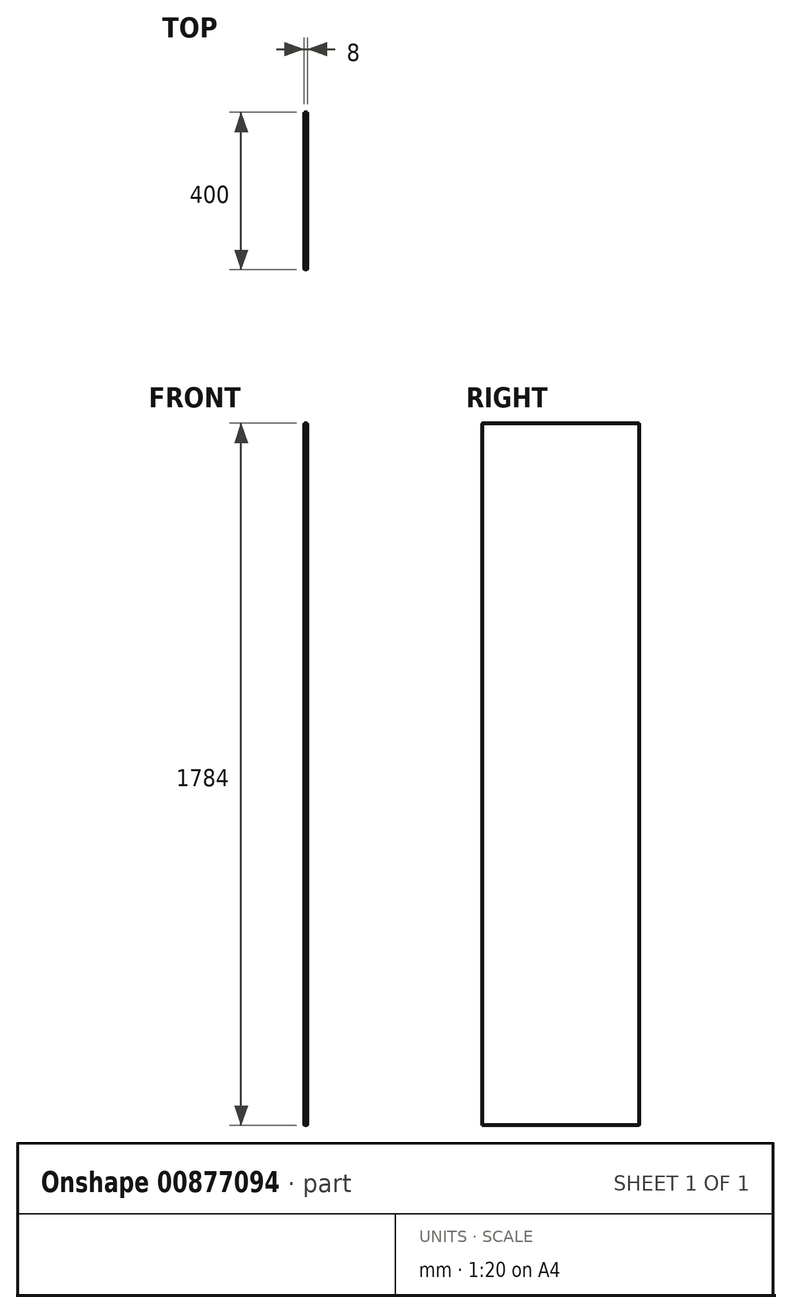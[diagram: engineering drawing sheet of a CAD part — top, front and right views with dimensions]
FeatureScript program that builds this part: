
annotation { "Feature Type Name" : "Feature", "Feature Type Description" : "" }
export const myFeature = defineFeature(function(context is Context, id is Id, definition is map)
    precondition{}
    {
        {
            var Q0;
            Q0=qCreatedBy(makeId("Right.planeOp"),FACE);
            var sketch = newSketch(context, id + "F0", { "sketchPlane" : qUnion([Q0])});
            skLineSegment(sketch, "E0.bottom", {"start": v(200, 892) * mm, "end": v(-200, 892) * mm});
            skLineSegment(sketch, "E0.top", {"start": v(200, -892) * mm, "end": v(-200, -892) * mm});
            skLineSegment(sketch, "E0.left", {"start": v(200, 892) * mm, "end": v(200, -892) * mm});
            skLineSegment(sketch, "E0.right", {"start": v(-200, 892) * mm, "end": v(-200, -892) * mm});
            skPoint(sketch, "E0.middle", {"position": v(0, 0) * mm});
            skSolve(sketch);
        }
        {
            var Q0;
            Q0=makeQuery(id+"F0.imprint","IMPRINT",FACE,{"disambiguationData":[TD([[makeQuery(id+"F0.imprint","IMPRINT",EDGE,{"derivedFrom":sQuery(id+"F0.wireOp",EDGE,"E0.bottom")}),1.0]])]});
            extrude(context, id + "F1", {"entities" : qUnion([Q0]), "endBound" : BoundingType.SYMMETRIC, "depth" : 8 * mm, "offsetDistance" : 25 * mm});
        }
        {
            var Q0;
            Q0=makeQuery(id+"F1.opExtrude","CAP_EDGE",EDGE,{"disambiguationData":[OSD([sQuery(id+"F0.wireOp",EDGE,"E0.left")])],"isStart":false});
            var Q1;
            Q1=makeQuery(id+"F1.opExtrude","CAP_EDGE",EDGE,{"disambiguationData":[OSD([sQuery(id+"F0.wireOp",EDGE,"E0.left")])],"isStart":true});
            var Q2;
            Q2=makeQuery(id+"F1.opExtrude","CAP_EDGE",EDGE,{"disambiguationData":[OSD([sQuery(id+"F0.wireOp",EDGE,"E0.bottom")])],"isStart":false});
            var Q3;
            Q3=makeQuery(id+"F1.opExtrude","CAP_EDGE",EDGE,{"disambiguationData":[OSD([sQuery(id+"F0.wireOp",EDGE,"E0.bottom")])],"isStart":true});
            var Q4;
            Q4=makeQuery(id+"F1.opExtrude","CAP_EDGE",EDGE,{"disambiguationData":[OSD([sQuery(id+"F0.wireOp",EDGE,"E0.top")])],"isStart":true});
            var Q5;
            Q5=makeQuery(id+"F1.opExtrude","CAP_EDGE",EDGE,{"disambiguationData":[OSD([sQuery(id+"F0.wireOp",EDGE,"E0.top")])],"isStart":false});
            var Q6;
            Q6=makeQuery(id+"F1.opExtrude","CAP_EDGE",EDGE,{"disambiguationData":[OSD([sQuery(id+"F0.wireOp",EDGE,"E0.right")])],"isStart":true});
            var Q7;
            Q7=makeQuery(id+"F1.opExtrude","CAP_EDGE",EDGE,{"disambiguationData":[OSD([sQuery(id+"F0.wireOp",EDGE,"E0.right")])],"isStart":false});
            chamfer(context, id + "F2", {"entities" : qUnion([Q0, Q1, Q2, Q3, Q4, Q5, Q6, Q7]), "width" : 1 * mm, "tangentPropagation" : true});
        }
        {
            var Q0;
            Q0=makeQuery(id+"F1.opExtrude","SWEPT_EDGE",EDGE,{"disambiguationData":[OSD([sQuery(id+"F0.wireOp",EDGE,"E0.top"),sQuery(id+"F0.wireOp",EDGE,"E0.left")])]});
            var Q1;
            Q1=makeQuery(id+"F1.opExtrude","SWEPT_EDGE",EDGE,{"disambiguationData":[OSD([sQuery(id+"F0.wireOp",EDGE,"E0.top"),sQuery(id+"F0.wireOp",EDGE,"E0.right")])]});
            var Q2;
            Q2=makeQuery(id+"F1.opExtrude","SWEPT_EDGE",EDGE,{"disambiguationData":[OSD([sQuery(id+"F0.wireOp",EDGE,"E0.bottom"),sQuery(id+"F0.wireOp",EDGE,"E0.right")])]});
            var Q3;
            Q3=makeQuery(id+"F1.opExtrude","SWEPT_EDGE",EDGE,{"disambiguationData":[OSD([sQuery(id+"F0.wireOp",EDGE,"E0.bottom"),sQuery(id+"F0.wireOp",EDGE,"E0.left")])]});
            chamfer(context, id + "F3", {"entities" : qUnion([Q0, Q1, Q2, Q3]), "width" : 1 * mm, "tangentPropagation" : true});
        }
    });
